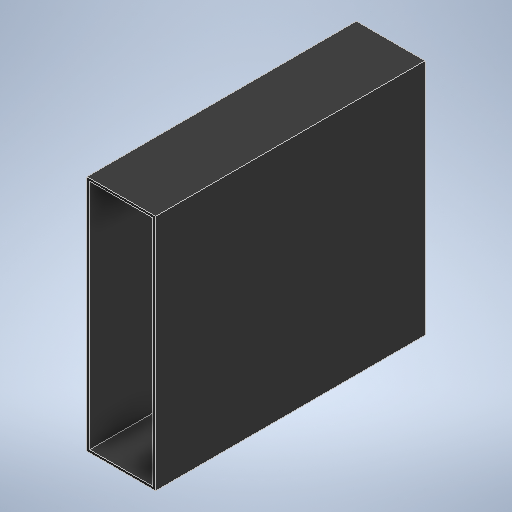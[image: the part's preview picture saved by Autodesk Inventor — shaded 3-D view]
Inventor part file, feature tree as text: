
AUTODESK INVENTOR PART (.ipt)
format: ipt  version: 2025 (Build 290162010, 162A)  size: 196,096 bytes
history: native  units: in
note: dims shown in document units (in); Inventor stores cm internally (conversion verified against a paired STEP export)
features: extrude x1, sketch x1
ambient origin geometry x8: Origin, YZ Plane, XZ Plane, XY Plane, X Axis, Y Axis, Z Axis, Center Point
bodies: Solid1 (feature_tree)
feature tree (2):
  extrude  "Extrusion1"  Depth=1.5in
  sketch  "Sketch1"  dims[d1=5.5in d2=1.5in d3=0.0625in d4=6.375in d5=0.0in]
